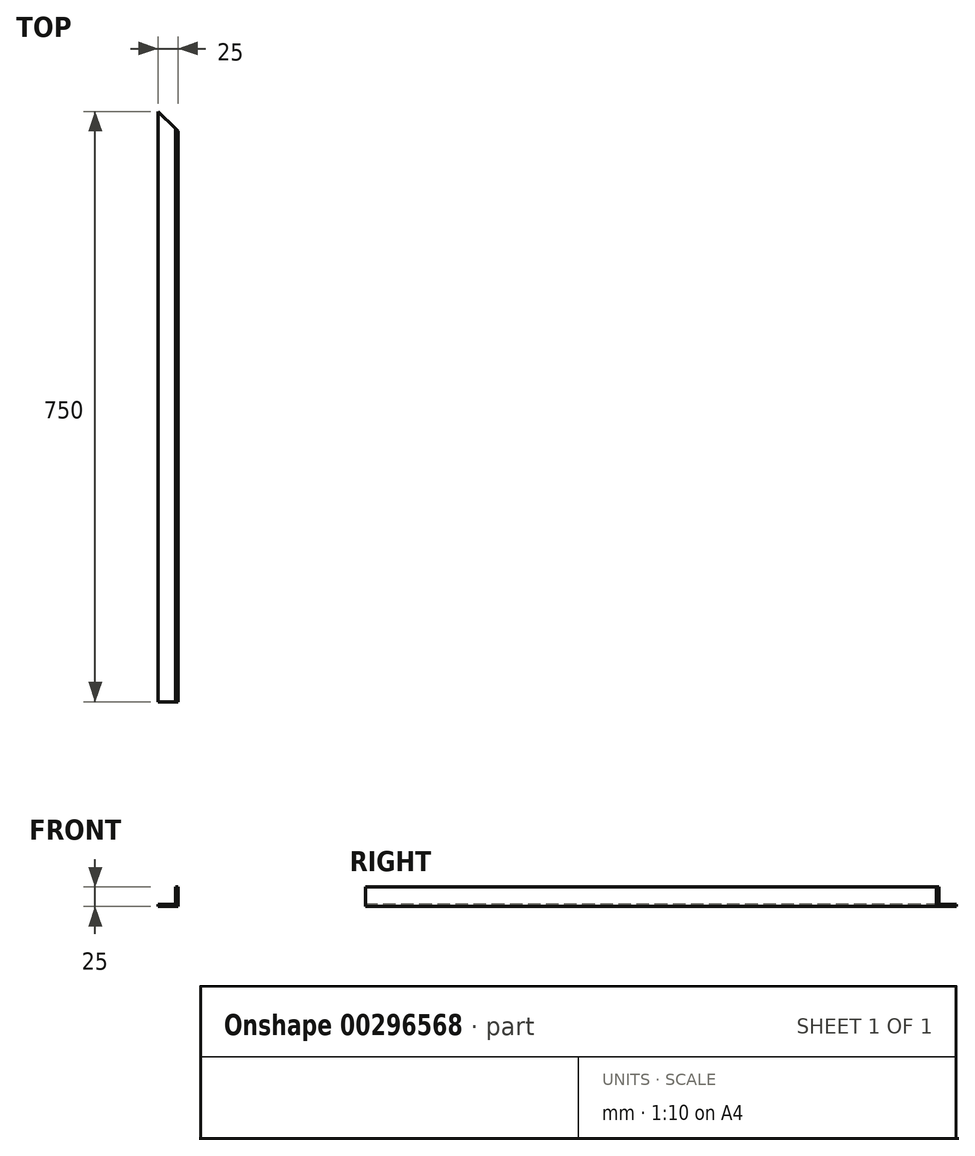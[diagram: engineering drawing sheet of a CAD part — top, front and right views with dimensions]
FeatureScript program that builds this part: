
annotation { "Feature Type Name" : "Feature", "Feature Type Description" : "" }
export const myFeature = defineFeature(function(context is Context, id is Id, definition is map)
    precondition{}
    {
        {
            var Q0;
            Q0=qCreatedBy(makeId("Front.planeOp"),FACE);
            var sketch = newSketch(context, id + "F0", { "sketchPlane" : qUnion([Q0])});
            skLineSegment(sketch, "E0", {"start": v(-16.97, -5.98) * mm, "end": v(5.03, -5.98) * mm});
            skLineSegment(sketch, "E1", {"start": v(5.03, -5.98) * mm, "end": v(5.03, 16.02) * mm});
            skLineSegment(sketch, "E2.0", {"start": v(8.03, -8.98) * mm, "end": v(8.03, 16.02) * mm});
            skLineSegment(sketch, "E2.1", {"start": v(-16.97, -8.98) * mm, "end": v(8.03, -8.98) * mm});
            skLineSegment(sketch, "E3", {"start": v(5.03, 16.02) * mm, "end": v(8.03, 16.02) * mm});
            skLineSegment(sketch, "E4", {"start": v(-16.97, -5.98) * mm, "end": v(-16.97, -8.98) * mm});
            skSolve(sketch);
        }
        {
            var Q0;
            Q0=makeQuery(id+"F0.imprint","IMPRINT",FACE,{"disambiguationData":[TD([[makeQuery(id+"F0.imprint","IMPRINT",EDGE,{"derivedFrom":sQuery(id+"F0.wireOp",EDGE,"E0")}),-1.0]])]});
            extrude(context, id + "F1", {"entities" : qUnion([Q0]), "depth" : 750 * mm});
        }
        {
            var Q0;
            Q0=makeQuery(id+"F1.opExtrude","SWEPT_FACE",FACE,{"disambiguationData":[OSD([sQuery(id+"F0.wireOp",EDGE,"E2.1")])]});
            var sketch = newSketch(context, id + "F2", { "sketchPlane" : qUnion([Q0])});
            skLineSegment(sketch, "E5", {"start": v(-16.97, 750) * mm, "end": v(8.03, 725) * mm});
            skLineSegment(sketch, "E6", {"start": v(8.03, 725) * mm, "end": v(8.03, 750) * mm});
            skSolve(sketch);
        }
        {
            var Q0;
            Q0=makeQuery(id+"F2.imprint","IMPRINT",FACE,{"disambiguationData":[TD([[makeQuery(id+"F2.imprint","IMPRINT",EDGE,{"derivedFrom":sQuery(id+"F2.wireOp",EDGE,"E5")}),1.0]])]});
            extrude(context, id + "F3", {"entities" : qUnion([Q0]), "operationType" : NewBodyOperationType.REMOVE, "oppositeDirection" : true, "depth" : 25 * mm});
        }
        {
            var Q0;
            Q0=makeQuery(id+"F1.opExtrude","SWEPT_BODY",BODY,{"disambiguationData":[OSD([sQuery(id+"F0.wireOp",EDGE,"E0"),sQuery(id+"F0.wireOp",EDGE,"E1"),sQuery(id+"F0.wireOp",EDGE,"E2.0"),sQuery(id+"F0.wireOp",EDGE,"E2.1"),sQuery(id+"F0.wireOp",EDGE,"E3"),sQuery(id+"F0.wireOp",EDGE,"E4")])]});
            var Q1;
            Q1=qCreatedBy(makeId("Front.planeOp"),FACE);
            mirror(context, id + "F4", {"entities" : qUnion([Q0]), "mirrorPlane" : qUnion([Q1])});
        }
        {
            var Q0;
            Q0=makeQuery(id+"F1.opExtrude","SWEPT_BODY",BODY,{"disambiguationData":[OSD([sQuery(id+"F0.wireOp",EDGE,"E0"),sQuery(id+"F0.wireOp",EDGE,"E1"),sQuery(id+"F0.wireOp",EDGE,"E2.0"),sQuery(id+"F0.wireOp",EDGE,"E2.1"),sQuery(id+"F0.wireOp",EDGE,"E3"),sQuery(id+"F0.wireOp",EDGE,"E4")])]});
            deleteBodies(context, id + "F5", {"entities" : qUnion([Q0])});
        }
    });
